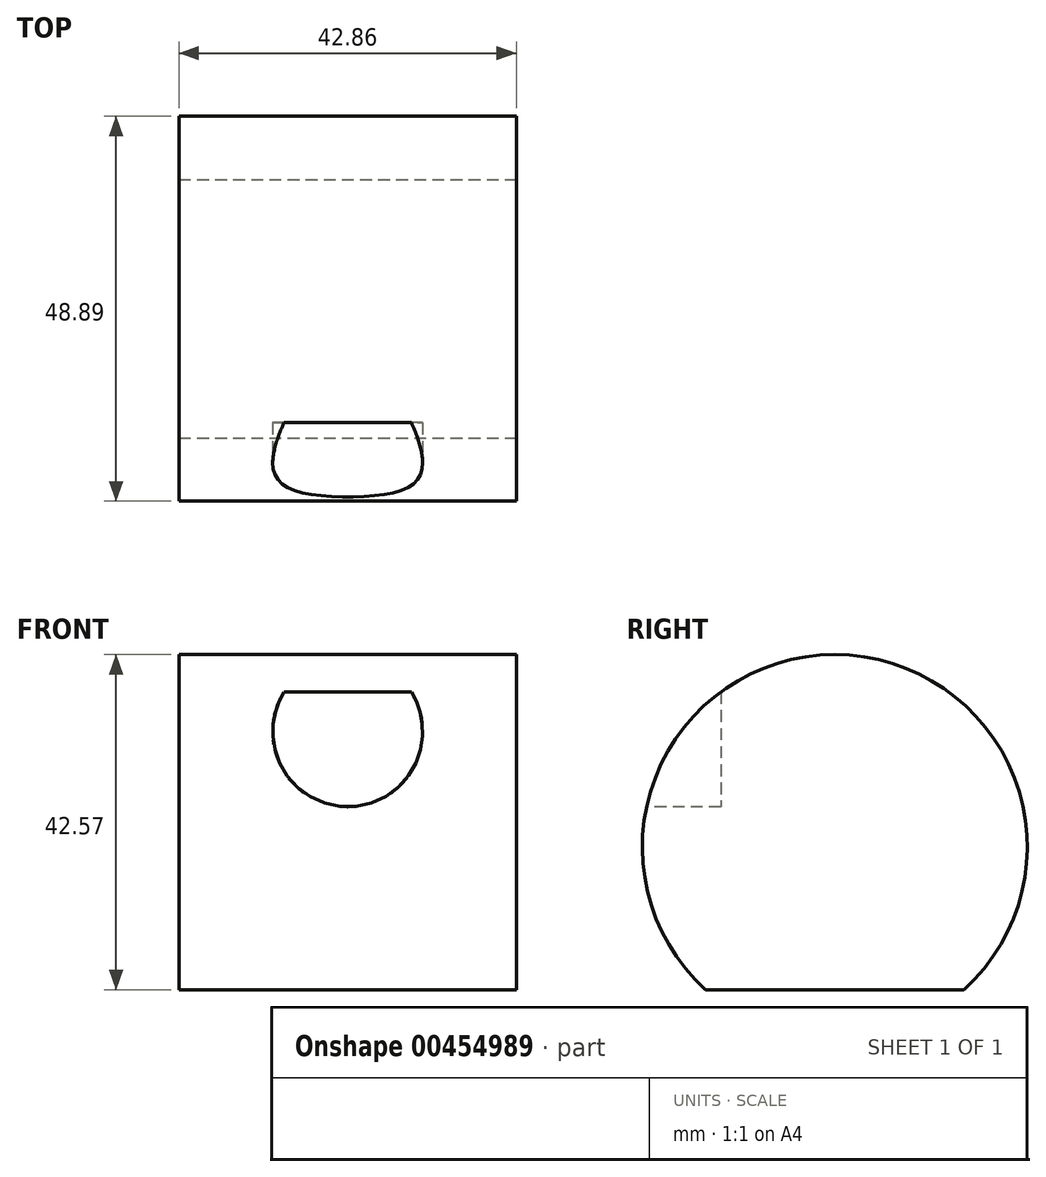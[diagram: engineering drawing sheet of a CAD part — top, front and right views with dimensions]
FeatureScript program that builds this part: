
annotation { "Feature Type Name" : "Feature", "Feature Type Description" : "" }
export const myFeature = defineFeature(function(context is Context, id is Id, definition is map)
    precondition{}
    {
        {
            var Q0;
            Q0=qCreatedBy(makeId("Right.planeOp"),FACE);
            var sketch = newSketch(context, id + "F0", { "sketchPlane" : qUnion([Q0])});
            skLineSegment(sketch, "E0", {"start": v(-152.4, 0) * mm, "end": v(152.4, 0) * mm});
            skLineSegment(sketch, "E1", {"start": v(-152.4, 0) * mm, "end": v(-152.4, 69.85) * mm});
            skLineSegment(sketch, "E2", {"start": v(152.4, 0) * mm, "end": v(152.4, 19.05) * mm});
            skLineSegment(sketch, "E3", {"start": v(152.4, 19.05) * mm, "end": v(-152.4, 69.85) * mm});
            skPoint(sketch, "E4.endSnap0", {"position": v(-152.4, 34.93) * mm});
            skLineSegment(sketch, "E5.0", {"start": v(-95.25, 50.8) * mm, "end": v(-152.4, 50.8) * mm, "construction": true});
            skLineSegment(sketch, "E5.1", {"start": v(-95.25, 50.8) * mm, "end": v(-95.25, 19.05) * mm, "construction": true});
            skLineSegment(sketch, "E5.2", {"start": v(-95.25, 19.05) * mm, "end": v(-152.4, 19.05) * mm, "construction": true});
            skSolve(sketch);
        }
        {
            var Q0;
            Q0=makeQuery(id+"F0.imprint","IMPRINT",FACE,{"disambiguationData":[TD([[makeQuery(id+"F0.imprint","IMPRINT",EDGE,{"derivedFrom":sQuery(id+"F0.wireOp",EDGE,"E0")}),1.0]])]});
            extrude(context, id + "F1", {"entities" : qUnion([Q0]), "depth" : 42.86 * mm, "symmetric" : true});
        }
        {
            var Q0;
            Q0=makeQuery(id+"F1.opExtrude","SWEPT_FACE",FACE,{"disambiguationData":[OSD([sQuery(id+"F0.wireOp",EDGE,"E1")])]});
            var sketch = newSketch(context, id + "F2", { "sketchPlane" : qUnion([Q0])});
            skLineSegment(sketch, "E6", {"start": v(21.43, 34.93) * mm, "end": v(0, 34.93) * mm, "construction": true});
            skCircle(sketch, "E7", {"center": v(0, 34.93) * mm, "radius": 9.53 * mm});
            skSolve(sketch);
        }
        {
            var Q0;
            Q0=makeQuery(id+"F2.imprint","IMPRINT",FACE,{"disambiguationData":[TD([[makeQuery(id+"F2.imprint","IMPRINT",EDGE,{"derivedFrom":sQuery(id+"F2.wireOp",EDGE,"E7")}),1.0]])]});
            var Q1;
            Q1=sQuery(id+"F2.wireOp",EDGE,"E7");
            extrude(context, id + "F3", {"entities" : qUnion([Q0]), "operationType" : NewBodyOperationType.REMOVE, "surfaceEntities" : qUnion([Q1]), "oppositeDirection" : true, "depth" : 50.8 * mm});
        }
        {
            var Q0;
            Q0=makeQuery(id+"F1.opExtrude","CAP_FACE",FACE,{"disambiguationData":[OSD([sQuery(id+"F0.wireOp",EDGE,"E0"),sQuery(id+"F0.wireOp",EDGE,"E1"),sQuery(id+"F0.wireOp",EDGE,"E2"),sQuery(id+"F0.wireOp",EDGE,"E3")])],"isStart":false});
            var sketch = newSketch(context, id + "F4", { "sketchPlane" : qUnion([Q0])});
            skLineSegment(sketch, "E8", {"start": v(-152.4, 34.93) * mm, "end": v(-152.4, 44.45) * mm, "construction": true});
            skLineSegment(sketch, "E9.0", {"start": v(-95.25, 19.05) * mm, "end": v(-152.4, 19.05) * mm, "construction": true});
            skLineSegment(sketch, "E9.1", {"start": v(-95.25, 50.8) * mm, "end": v(-95.25, 19.05) * mm, "construction": true});
            skLineSegment(sketch, "E9.2", {"start": v(-152.4, 50.8) * mm, "end": v(-95.25, 50.8) * mm, "construction": true});
            skLineSegment(sketch, "E10", {"start": v(57.15, 0) * mm, "end": v(57.15, 34.93) * mm, "construction": true});
            skLineSegment(sketch, "E11", {"start": v(-152.4, 44.45) * mm, "end": v(-101.6, 44.45) * mm, "construction": true});
            skLineSegment(sketch, "E12", {"start": v(-101.6, 44.45) * mm, "end": v(-101.6, 25.4) * mm, "construction": true});
            skLineSegment(sketch, "E13", {"start": v(-101.6, 25.4) * mm, "end": v(-152.4, 25.4) * mm, "construction": true});
            skLineSegment(sketch, "E14", {"start": v(-152.4, 2.16) * mm, "end": v(63.37, 2.16) * mm});
            skLineSegment(sketch, "E15", {"start": v(63.37, 2.16) * mm, "end": v(63.37, 11.05) * mm});
            skPoint(sketch, "E16.endSnap0", {"position": v(0, 44.45) * mm});
            skFitSpline(sketch, "E17", {"points": [v(63.37, 11.05) * mm, v(-51.25, 21.75) * mm], "startDerivative": vector(-78.99, 29.04) * mm, "endDerivative": vector(-55.2, 61.13) * mm});
            skFitSpline(sketch, "E18", {"points": [v(-51.25, 21.75) * mm, v(-78, 51.14) * mm, v(-152.4, 55.33) * mm, v(-152.4, 56.57) * mm], "startDerivative": vector(-93.89, 42.14) * mm, "endDerivative": vector(4.07, 7.3) * mm});
            skCircle(sketch, "E19", {"center": v(-131.91, 11.69) * mm, "radius": 1.59 * mm});
            skCircle(sketch, "E20", {"center": v(22.35, 11.69) * mm, "radius": 1.59 * mm});
            skFitSpline(sketch, "E21", {"points": [v(48.47, 13.7) * mm, v(30.98, 17.26) * mm, v(21.63, 18.46) * mm, v(8.44, 14.86) * mm, v(-18.2, 12.04) * mm], "startDerivative": vector(-72.56, 14.16) * mm, "endDerivative": vector(-90.08, -4.68) * mm});
            skFitSpline(sketch, "E22.trimOffspring", {"points": [v(63.37, 11.05) * mm, v(-51.25, 21.75) * mm], "startDerivative": vector(-78.99, 29.04) * mm, "endDerivative": vector(-55.2, 61.13) * mm});
            skCircle(sketch, "E23", {"center": v(-87.11, 20.28) * mm, "radius": 39.28 * mm});
            skCircle(sketch, "E24", {"center": v(-87.11, 20.28) * mm, "radius": 24.45 * mm});
            skSolve(sketch);
        }
        {
            var Q0;
            {var subQ4=sQuery(id+"F4.wireOp",EDGE,"E14");Q0=makeQuery(id+"F4.imprint","IMPRINT",FACE,{"disambiguationData":[TD([[makeQuery(id+"F4.imprint","IMPRINT",EDGE,{"derivedFrom":subQ4}),1.0]])]});}
            extrude(context, id + "F5", {"entities" : qUnion([Q0]), "operationType" : NewBodyOperationType.INTERSECT, "endBound" : BoundingType.THROUGH_ALL, "oppositeDirection" : true, "depth" : 25.4 * mm});
        }
    });
